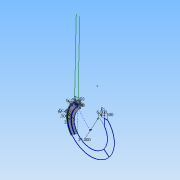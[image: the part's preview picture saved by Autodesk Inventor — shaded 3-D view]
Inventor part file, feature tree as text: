
AUTODESK INVENTOR PART (.ipt)
format: ipt  version: 2013 (Build 170138000, 138)  size: 154,112 bytes
history: native  units: in
note: dims shown in document units (in); Inventor stores cm internally (conversion verified against a paired STEP export)
features: reference x3, extrude x2, plane x1, other x1, sketch x1
ambient origin geometry x8: Origin, YZ Plane, XZ Plane, XY Plane, X Axis, Y Axis, Z Axis, Center Point
bodies: Solid3 (feature_tree)
feature tree (8):
  plane  "Work Plane1"
  extrude  "Extrusion6"  Depth=2.5in
  extrude  "Extrusion7"  Depth=33.0in
  other  "ThermoBulbBorder"
  reference  "Reference2"
  reference  "Reference3"
  reference  "Reference4"
  sketch  "Sketch3"  dims[d0=24.0in d5=2.5in d6=2.5in d7=33.0in d8=0.48in d9=0.48in d10=2.25in d11=1.61in d12=6.0in d20=0.5in d38=0.48in d39=2.25in d53=4.25in d54=0.71in d55=0.0in d56=0.5in d57=0.48in d58=2.25in d60=0.48in d61=2.5in d62=0.25in d63=0.48in d64=0.76in d65=1.24in d66=0.76in d67=1.24in d68=2.25in d69=0.48in d70=0.5in d71=0.0in]
